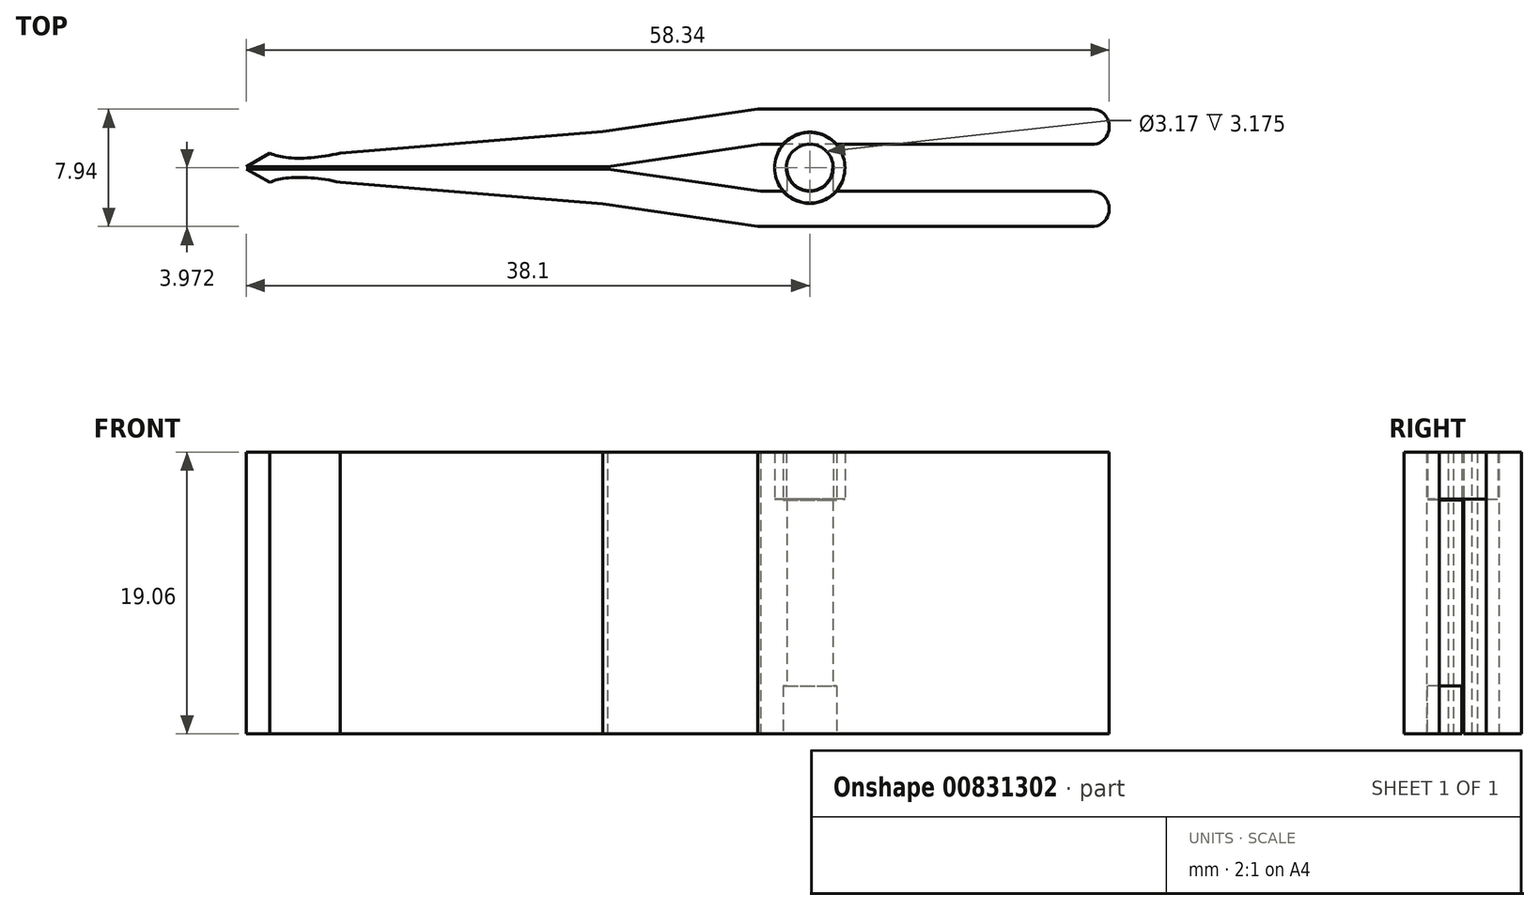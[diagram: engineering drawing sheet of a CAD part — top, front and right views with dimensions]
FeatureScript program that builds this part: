
annotation { "Feature Type Name" : "Feature", "Feature Type Description" : "" }
export const myFeature = defineFeature(function(context is Context, id is Id, definition is map)
    precondition{}
    {
        {
            var Q0;
            Q0=qCreatedBy(makeId("Top.planeOp"),FACE);
            var sketch = newSketch(context, id + "F0", { "sketchPlane" : qUnion([Q0])});
            skLineSegment(sketch, "E0", {"start": v(19.05, 0) * mm, "end": v(-3.34, 0) * mm});
            skFitSpline(sketch, "E1", {"points": [v(19.05, 2.38) * mm, v(19.05, 0) * mm], "startDerivative": vector(4.76, 0) * mm, "endDerivative": vector(-4.76, 0) * mm});
            skLineSegment(sketch, "E2", {"start": v(19.05, 2.38) * mm, "end": v(20.64, 2.38) * mm, "construction": true});
            skLineSegment(sketch, "E3", {"start": v(20.64, 2.38) * mm, "end": v(20.64, 0) * mm, "construction": true});
            skLineSegment(sketch, "E4", {"start": v(20.64, 0) * mm, "end": v(19.05, 0) * mm, "construction": true});
            skLineSegment(sketch, "E5", {"start": v(19.05, 2.38) * mm, "end": v(-3.51, 2.38) * mm});
            skFitSpline(sketch, "E6.MirrorCS", {"points": [v(19.05, -5.56) * mm, v(19.05, -3.17) * mm], "startDerivative": vector(4.76, 0) * mm, "endDerivative": vector(-4.76, 0) * mm});
            skLineSegment(sketch, "E7.MirrorCS", {"start": v(20.64, -3.18) * mm, "end": v(19.05, -3.17) * mm, "construction": true});
            skLineSegment(sketch, "E8.MirrorCS", {"start": v(19.05, -5.56) * mm, "end": v(20.64, -5.56) * mm, "construction": true});
            skLineSegment(sketch, "E9.MirrorCS", {"start": v(19.05, -3.17) * mm, "end": v(-3.34, -3.17) * mm});
            skLineSegment(sketch, "E10", {"start": v(20.64, -5.56) * mm, "end": v(20.64, -3.18) * mm, "construction": true});
            skLineSegment(sketch, "E11", {"start": v(0, 0) * mm, "end": v(0, -3.18) * mm, "construction": true});
            skLineSegment(sketch, "E12", {"start": v(21.44, -1.59) * mm, "end": v(-56.65, -1.59) * mm, "construction": true});
            skPoint(sketch, "E12.startSnap0", {"position": v(0, -1.59) * mm});
            skCircle(sketch, "E13", {"center": v(0, -1.59) * mm, "radius": 2.38 * mm});
            skCircle(sketch, "E14", {"center": v(0, -1.59) * mm, "radius": 2.41 * mm});
            skCircle(sketch, "E15", {"center": v(0, -1.59) * mm, "radius": 1.59 * mm});
            skCircle(sketch, "E16", {"center": v(0, -1.59) * mm, "radius": 1.55 * mm});
            skLineSegment(sketch, "E17", {"start": v(-13.66, -1.51) * mm, "end": v(-38.1, -1.51) * mm});
            skLineSegment(sketch, "E18", {"start": v(-38.1, -1.51) * mm, "end": v(-36.51, -0.6) * mm});
            skLineSegment(sketch, "E19", {"start": v(-36.51, -0.6) * mm, "end": v(-31.75, -0.6) * mm, "construction": true});
            skFitSpline(sketch, "E20", {"points": [v(-36.51, -0.6) * mm, v(-31.75, -0.6) * mm], "startDerivative": vector(2.79, -1.37) * mm, "endDerivative": vector(5.8, 1.37) * mm});
            skLineSegment(sketch, "E21", {"start": v(-3.34, 0) * mm, "end": v(-13.66, -1.51) * mm});
            skLineSegment(sketch, "E22", {"start": v(-3.34, -3.17) * mm, "end": v(-13.66, -1.66) * mm});
            skLineSegment(sketch, "E23", {"start": v(-13.66, -1.66) * mm, "end": v(-38.1, -1.66) * mm});
            skLineSegment(sketch, "E24", {"start": v(-38.1, -1.66) * mm, "end": v(-36.51, -2.58) * mm});
            skLineSegment(sketch, "E25", {"start": v(-36.51, -2.58) * mm, "end": v(-31.75, -2.58) * mm, "construction": true});
            skFitSpline(sketch, "E26", {"points": [v(-36.51, -2.58) * mm, v(-31.75, -2.58) * mm], "startDerivative": vector(2.79, 1.37) * mm, "endDerivative": vector(5.8, -1.37) * mm});
            skLineSegment(sketch, "E27.0", {"start": v(-3.51, 2.38) * mm, "end": v(-14, 0.85) * mm});
            skLineSegment(sketch, "E28", {"start": v(-14, 0.85) * mm, "end": v(-31.75, -0.6) * mm});
            skLineSegment(sketch, "E29", {"start": v(-3.51, 2.38) * mm, "end": v(-3.51, -8.38) * mm, "construction": true});
            skLineSegment(sketch, "E30", {"start": v(-14, 0.85) * mm, "end": v(-14, -10.35) * mm, "construction": true});
            skLineSegment(sketch, "E31", {"start": v(19.05, -5.56) * mm, "end": v(-3.51, -5.56) * mm});
            skLineSegment(sketch, "E32", {"start": v(-3.51, -5.56) * mm, "end": v(-14, -4.02) * mm});
            skPoint(sketch, "E32.endSnap0", {"position": v(-14, -4.75) * mm});
            skLineSegment(sketch, "E33", {"start": v(-14, -4.02) * mm, "end": v(-31.75, -2.58) * mm});
            skSolve(sketch);
        }
        {
            var Q0;
            {var subQ4=sQuery(id+"F0.wireOp",EDGE,"E6.MirrorCS");Q0=makeQuery(id+"F0.imprint","IMPRINT",FACE,{"disambiguationData":[TD([[makeQuery(id+"F0.imprint","IMPRINT",EDGE,{"derivedFrom":subQ4}),1.0]])]});}
            var Q1;
            {var subQ0=sQuery(id+"F0.wireOp",EDGE,"E1");Q1=makeQuery(id+"F0.imprint","IMPRINT",FACE,{"disambiguationData":[TD([[makeQuery(id+"F0.imprint","IMPRINT",EDGE,{"derivedFrom":subQ0}),-1.0]])]});}
            extrude(context, id + "F1", {"entities" : qUnion([Q0, Q1]), "endBound" : BoundingType.SYMMETRIC, "depth" : 19.05 * mm, "offsetDistance" : 25.4 * mm});
        }
        {
            var Q0;
            {var subQ0=sQuery(id+"F0.wireOp",EDGE,"E13");var subQ1=sQuery(id+"F0.wireOp",EDGE,"E0");var subQ2=makeQuery(id+"F0.imprint","INTERSECT",VERTEX,{"disambiguationData":[OD(0.0)],"derivedFrom":[subQ1,subQ0]});Q0=makeQuery(id+"F0.imprint","IMPRINT",FACE,{"disambiguationData":[TD([[makeQuery(id+"F0.imprint","IMPRINT",EDGE,{"disambiguationData":[TD([[subQ2,-1.0]])],"derivedFrom":subQ1}),-1.0]])]});}
            var Q1;
            {var subQ0=sQuery(id+"F0.wireOp",EDGE,"E14");var subQ1=sQuery(id+"F0.wireOp",EDGE,"E0");var subQ2=makeQuery(id+"F0.imprint","INTERSECT",VERTEX,{"disambiguationData":[OD(0.0)],"derivedFrom":[subQ1,subQ0]});Q1=makeQuery(id+"F0.imprint","IMPRINT",FACE,{"disambiguationData":[TD([[makeQuery(id+"F0.imprint","IMPRINT",EDGE,{"disambiguationData":[TD([[subQ2,-1.0]])],"derivedFrom":subQ1}),-1.0]])]});}
            extrude(context, id + "F2", {"entities" : qUnion([Q0, Q1]), "endBound" : BoundingType.SYMMETRIC, "depth" : 12.7 * mm, "offsetDistance" : 25.4 * mm});
        }
        {
            var Q0;
            Q0=makeQuery(id+"F1.opExtrude","SWEPT_BODY",BODY,{"disambiguationData":[OSD([sQuery(id+"F0.wireOp",EDGE,"E0"),sQuery(id+"F0.wireOp",EDGE,"E1"),sQuery(id+"F0.wireOp",EDGE,"qeccKUcQ-3vMP-5g8q-NfE8-jC8HM5mCseAS"),sQuery(id+"F0.wireOp",EDGE,"d6318fa1-6fe5-4666-b0b6-6479e8210f40"),sQuery(id+"F0.wireOp",EDGE,"E5"),sQuery(id+"F0.wireOp",EDGE,"dL6aYxVl-xdIL-pu46-SImy-4reyTvtszrQX"),sQuery(id+"F0.wireOp",EDGE,"zCCRS7Mm-aioU-Ri8N-ycMK-PwaVGb7OzPh1"),sQuery(id+"F0.wireOp",EDGE,"cr6eNREQ-uAZy-lqhM-RrFl-UblUkAwWfTPr"),sQuery(id+"F0.wireOp",EDGE,"E14")])]});
            var Q1;
            Q1=makeQuery(id+"F2.opExtrude","SWEPT_BODY",BODY,{"disambiguationData":[OSD([sQuery(id+"F0.wireOp",EDGE,"E0"),sQuery(id+"F0.wireOp",EDGE,"E14")])]});
            booleanBodies(context, id + "F3", {"operationType" : BooleanOperationType.UNION, "tools" : qUnion([Q0, Q1])});
        }
        {
            var Q0;
            Q0=makeQuery(id+"F2.opExtrude","CAP_FACE",FACE,{"disambiguationData":[OSD([sQuery(id+"F0.wireOp",EDGE,"E0"),sQuery(id+"F0.wireOp",EDGE,"E14")])],"isStart":false});
            var sketch = newSketch(context, id + "F4", { "sketchPlane" : qUnion([Q0])});
            skCircle(sketch, "E34", {"center": v(0, -1.59) * mm, "radius": 2.38 * mm});
            skCircle(sketch, "E35", {"center": v(0, -1.59) * mm, "radius": 1.59 * mm});
            skSolve(sketch);
        }
        {
            var Q0;
            {var subQ4=sQuery(id+"F4.wireOp",EDGE,"E35");Q0=makeQuery(id+"F4.imprint","IMPRINT",FACE,{"disambiguationData":[TD([[makeQuery(id+"F4.imprint","IMPRINT",EDGE,{"derivedFrom":subQ4}),-1.0]])]});}
            var Q1;
            {var subQ0=sQuery(id+"F4.wireOp",EDGE,"E34");var subQ1=makeQuery(id+"F2.opExtrude","CAP_EDGE",EDGE,{"disambiguationData":[OSD([sQuery(id+"F0.wireOp",EDGE,"E0")])],"isStart":false});var subQ2=makeQuery(id+"F4.imprint","INTERSECT",VERTEX,{"disambiguationData":[OD(0.0)],"derivedFrom":[subQ1,subQ0]});Q1=makeQuery(id+"F4.imprint","IMPRINT",FACE,{"disambiguationData":[TD([[makeQuery(id+"F4.imprint","IMPRINT",EDGE,{"disambiguationData":[TD([[subQ2,-1.0]])],"derivedFrom":subQ0}),1.0]])]});}
            extrude(context, id + "F5", {"entities" : qUnion([Q0, Q1]), "operationType" : NewBodyOperationType.ADD, "depth" : 3.17 * mm, "offsetDistance" : 25.4 * mm});
        }
        {
            var Q0;
            Q0=qCreatedBy(makeId("Top.planeOp"),FACE);
            var sketch = newSketch(context, id + "F6", { "sketchPlane" : qUnion([Q0])});
            skLineSegment(sketch, "E36", {"start": v(0, 0) * mm, "end": v(0, -1.59) * mm, "construction": true});
            skLineSegment(sketch, "E37", {"start": v(0, -1.59) * mm, "end": v(1.55, -1.59) * mm, "construction": true});
            skLineSegment(sketch, "E38", {"start": v(0, -1.59) * mm, "end": v(-1.55, -1.59) * mm, "construction": true});
            skLineSegment(sketch, "E39", {"start": v(0, -1.59) * mm, "end": v(0, -3.18) * mm, "construction": true});
            skLineSegment(sketch, "E40", {"start": v(2.87, -3.18) * mm, "end": v(-2.47, -3.18) * mm, "construction": true});
            skLineSegment(sketch, "E41", {"start": v(-1.55, -1.59) * mm, "end": v(-1.55, -3.18) * mm});
            skLineSegment(sketch, "E42", {"start": v(1.55, -1.59) * mm, "end": v(1.55, -3.18) * mm});
            skLineSegment(sketch, "E43", {"start": v(1.55, -3.18) * mm, "end": v(-1.55, -3.18) * mm});
            skLineSegment(sketch, "E44", {"start": v(0, -1.59) * mm, "end": v(0, -3.14) * mm, "construction": true});
            skArc(sketch, "E45", {"start": v(-1.55, -1.59) * mm, "mid": v(0, -3.14) * mm, "end": v(1.55, -1.59) * mm});
            skLineSegment(sketch, "E46", {"start": v(0, -1.59) * mm, "end": v(0, -4) * mm, "construction": true});
            skLineSegment(sketch, "E47", {"start": v(0, -1.59) * mm, "end": v(2.41, -1.59) * mm, "construction": true});
            skLineSegment(sketch, "E48", {"start": v(0, -1.59) * mm, "end": v(-2.41, -1.59) * mm, "construction": true});
            skArc(sketch, "E49", {"start": v(-2.41, -1.59) * mm, "mid": v(0, -4) * mm, "end": v(2.41, -1.59) * mm});
            skSolve(sketch);
        }
        {
            var Q0;
            Q0 = qSketchRegion(id + "F6", true);
            var Q1;
            {var subQ0=sQuery(id+"F0.wireOp",EDGE,"E13");var subQ1=sQuery(id+"F0.wireOp",EDGE,"E9.MirrorCS");var subQ2=makeQuery(id+"F0.imprint","INTERSECT",VERTEX,{"disambiguationData":[OD(0.0)],"derivedFrom":[subQ1,subQ0]});Q1=makeQuery(id+"F0.imprint","IMPRINT",FACE,{"disambiguationData":[TD([[makeQuery(id+"F0.imprint","IMPRINT",EDGE,{"disambiguationData":[TD([[subQ2,-1.0]])],"derivedFrom":subQ1}),1.0]])]});}
            var Q2;
            {var subQ0=sQuery(id+"F0.wireOp",EDGE,"E14");var subQ1=sQuery(id+"F0.wireOp",EDGE,"E9.MirrorCS");var subQ2=makeQuery(id+"F0.imprint","INTERSECT",VERTEX,{"disambiguationData":[OD(0.0)],"derivedFrom":[subQ1,subQ0]});Q2=makeQuery(id+"F0.imprint","IMPRINT",FACE,{"disambiguationData":[TD([[makeQuery(id+"F0.imprint","IMPRINT",EDGE,{"disambiguationData":[TD([[subQ2,-1.0]])],"derivedFrom":subQ1}),1.0]])]});}
            extrude(context, id + "F7", {"entities" : qUnion([Q0, Q1, Q2]), "operationType" : NewBodyOperationType.ADD, "endBound" : BoundingType.SYMMETRIC, "depth" : 12.57 * mm, "offsetDistance" : 25.4 * mm});
        }
        {
            var Q0;
            Q0=makeQuery(id+"F2.opExtrude","CAP_FACE",FACE,{"disambiguationData":[OSD([sQuery(id+"F0.wireOp",EDGE,"E0"),sQuery(id+"F0.wireOp",EDGE,"E14")])],"isStart":true});
            var sketch = newSketch(context, id + "F8", { "sketchPlane" : qUnion([Q0])});
            skCircle(sketch, "E50", {"center": v(0, 1.59) * mm, "radius": 2.38 * mm});
            skCircle(sketch, "E51", {"center": v(0, 1.59) * mm, "radius": 1.59 * mm});
            skSolve(sketch);
        }
        {
            var Q0;
            {var subQ0=sQuery(id+"F8.wireOp",EDGE,"E50");Q0=makeQuery(id+"F8.imprint","IMPRINT",FACE,{"disambiguationData":[TD([[makeQuery(id+"F8.imprint","IMPRINT",EDGE,{"disambiguationData":[OD(0.0)],"derivedFrom":subQ0}),-1.0]])]});}
            var Q1;
            {var subQ0=sQuery(id+"F8.wireOp",EDGE,"E50");Q1=makeQuery(id+"F8.imprint","IMPRINT",FACE,{"disambiguationData":[TD([[makeQuery(id+"F8.imprint","IMPRINT",EDGE,{"disambiguationData":[OD(1.0)],"derivedFrom":subQ0}),1.0]])]});}
            extrude(context, id + "F9", {"entities" : qUnion([Q0, Q1]), "operationType" : NewBodyOperationType.ADD, "depth" : 3.17 * mm, "offsetDistance" : 25.4 * mm});
        }
    });
